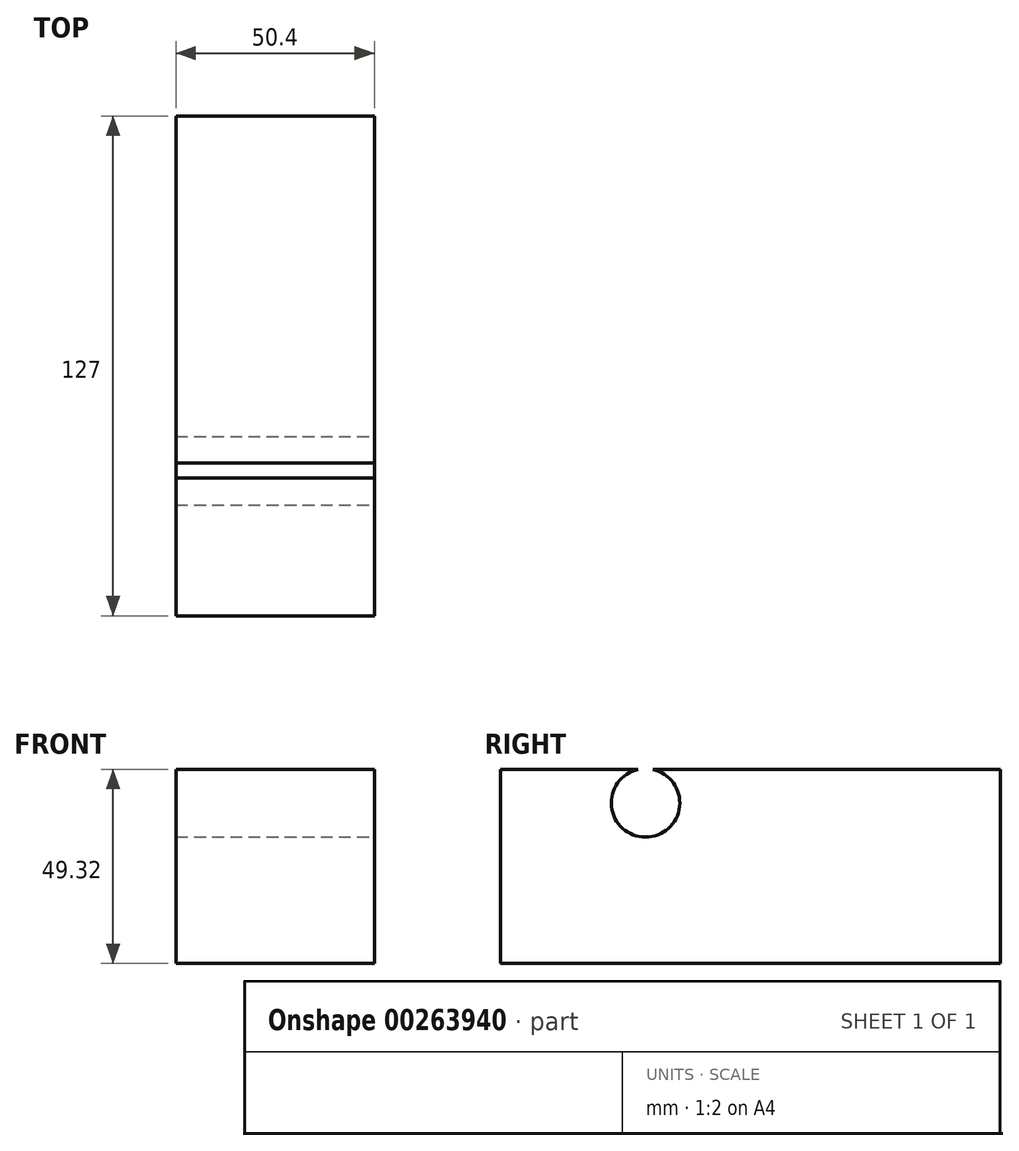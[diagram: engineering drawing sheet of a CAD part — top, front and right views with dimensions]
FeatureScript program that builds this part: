
annotation { "Feature Type Name" : "Feature", "Feature Type Description" : "" }
export const myFeature = defineFeature(function(context is Context, id is Id, definition is map)
    precondition{}
    {
        {
            var Q0;
            Q0=qCreatedBy(makeId("Front.planeOp"),FACE);
            var sketch = newSketch(context, id + "F0", { "sketchPlane" : qUnion([Q0])});
            skLineSegment(sketch, "E0.bottom", {"start": v(0, 0) * mm, "end": v(50.4, 0) * mm});
            skLineSegment(sketch, "E0.top", {"start": v(0, 49.32) * mm, "end": v(50.4, 49.32) * mm});
            skLineSegment(sketch, "E0.left", {"start": v(0, 0) * mm, "end": v(0, 49.32) * mm});
            skLineSegment(sketch, "E0.right", {"start": v(50.4, 0) * mm, "end": v(50.4, 49.32) * mm});
            skSolve(sketch);
        }
        {
            var Q0;
            Q0=makeQuery(id+"F0.imprint","IMPRINT",FACE,{"disambiguationData":[TD([[makeQuery(id+"F0.imprint","IMPRINT",EDGE,{"derivedFrom":sQuery(id+"F0.wireOp",EDGE,"E0.bottom")}),1.0]])]});
            extrude(context, id + "F1", {"entities" : qUnion([Q0]), "oppositeDirection" : true, "depth" : 127 * mm});
        }
        {
            var Q0;
            Q0=makeQuery(id+"F1.opExtrude","SWEPT_FACE",FACE,{"disambiguationData":[OSD([sQuery(id+"F0.wireOp",EDGE,"E0.right")])]});
            var sketch = newSketch(context, id + "F2", { "sketchPlane" : qUnion([Q0])});
            skCircle(sketch, "E1", {"center": v(36.89, 40.82) * mm, "radius": 8.7 * mm});
            skSolve(sketch);
        }
        {
            var Q0;
            {var subQ0=sQuery(id+"F2.wireOp",EDGE,"E1");var subQ1=makeQuery(id+"F1.opExtrude","SWEPT_EDGE",EDGE,{"disambiguationData":[OSD([sQuery(id+"F0.wireOp",EDGE,"E0.top"),sQuery(id+"F0.wireOp",EDGE,"E0.right")])]});var subQ2=makeQuery(id+"F2.imprint","INTERSECT",VERTEX,{"disambiguationData":[OD(0.0)],"derivedFrom":[subQ1,subQ0]});Q0=makeQuery(id+"F2.imprint","IMPRINT",FACE,{"disambiguationData":[TD([[makeQuery(id+"F2.imprint","IMPRINT",EDGE,{"disambiguationData":[TD([[subQ2,-1.0]])],"derivedFrom":subQ0}),1.0]])]});}
            extrude(context, id + "F3", {"entities" : qUnion([Q0]), "operationType" : NewBodyOperationType.REMOVE, "endBound" : BoundingType.UP_TO_NEXT, "oppositeDirection" : true, "depth" : 50.8 * mm});
        }
    });
